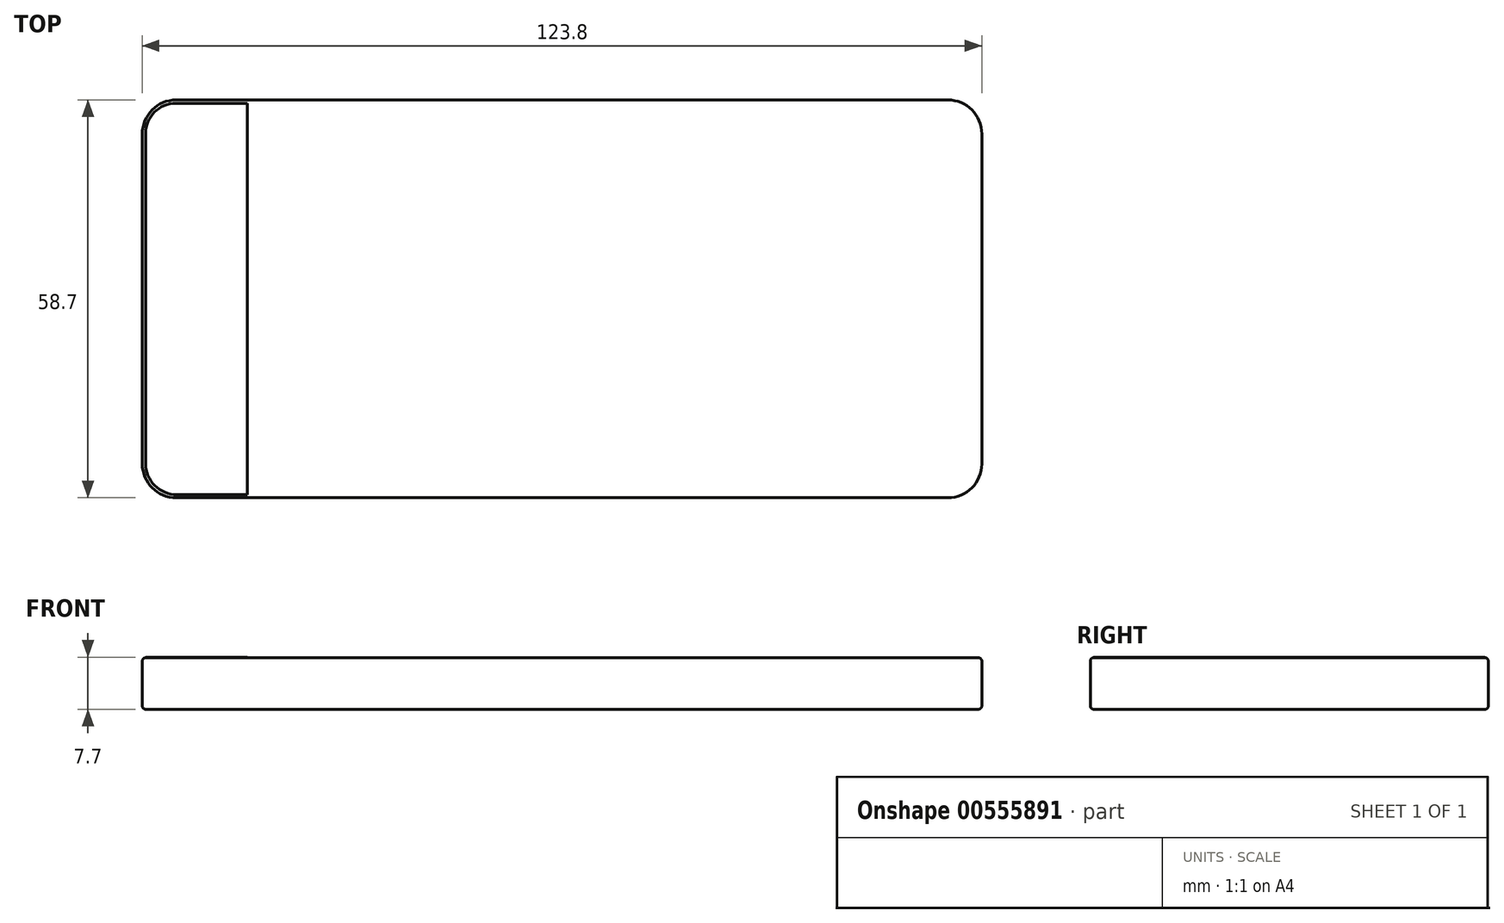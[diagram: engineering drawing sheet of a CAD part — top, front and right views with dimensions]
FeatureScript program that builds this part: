
annotation { "Feature Type Name" : "Feature", "Feature Type Description" : "" }
export const myFeature = defineFeature(function(context is Context, id is Id, definition is map)
    precondition{}
    {
        {
            var Q0;
            Q0=qCreatedBy(makeId("Top.planeOp"),FACE);
            var sketch = newSketch(context, id + "F0", { "sketchPlane" : qUnion([Q0])});
            skLineSegment(sketch, "E0.bottom", {"start": v(-53.09, -10.18) * mm, "end": v(60.71, -10.18) * mm});
            skLineSegment(sketch, "E0.top", {"start": v(-53.09, 48.52) * mm, "end": v(60.71, 48.52) * mm});
            skLineSegment(sketch, "E0.left", {"start": v(-58.09, -5.18) * mm, "end": v(-58.09, 43.52) * mm});
            skLineSegment(sketch, "E0.right", {"start": v(65.71, -5.18) * mm, "end": v(65.71, 43.52) * mm});
            skPoint(sketch, "E1.visualSharp", {"position": v(-58.09, -10.18) * mm});
            skArc(sketch, "E1.filletArc", {"start": v(-58.09, -5.18) * mm, "mid": v(-56.62, -8.71) * mm, "end": v(-53.09, -10.18) * mm});
            skPoint(sketch, "E2.visualSharp", {"position": v(-58.09, 48.52) * mm});
            skArc(sketch, "E2.filletArc", {"start": v(-53.09, 48.52) * mm, "mid": v(-56.62, 47.06) * mm, "end": v(-58.09, 43.52) * mm});
            skPoint(sketch, "E3.visualSharp", {"position": v(65.71, 48.52) * mm});
            skArc(sketch, "E3.filletArc", {"start": v(65.71, 43.52) * mm, "mid": v(64.25, 47.06) * mm, "end": v(60.71, 48.52) * mm});
            skPoint(sketch, "E4.visualSharp", {"position": v(65.71, -10.18) * mm});
            skArc(sketch, "E4.filletArc", {"start": v(60.71, -10.18) * mm, "mid": v(64.25, -8.71) * mm, "end": v(65.71, -5.18) * mm});
            skSolve(sketch);
        }
        {
            var Q0;
            Q0=makeQuery(id+"F0.imprint","IMPRINT",FACE,{"disambiguationData":[TD([[makeQuery(id+"F0.imprint","IMPRINT",EDGE,{"derivedFrom":sQuery(id+"F0.wireOp",EDGE,"E0.bottom")}),1.0]])]});
            extrude(context, id + "F1", {"entities" : qUnion([Q0]), "depth" : 7.6 * mm, "offsetDistance" : 25 * mm});
        }
        {
            var Q0;
            Q0=makeQuery(id+"F1.opExtrude","CAP_FACE",FACE,{"disambiguationData":[OSD([sQuery(id+"F0.wireOp",EDGE,"E0.bottom"),sQuery(id+"F0.wireOp",EDGE,"E0.top"),sQuery(id+"F0.wireOp",EDGE,"E0.left"),sQuery(id+"F0.wireOp",EDGE,"E0.right"),sQuery(id+"F0.wireOp",EDGE,"E1.filletArc"),sQuery(id+"F0.wireOp",EDGE,"E2.filletArc"),sQuery(id+"F0.wireOp",EDGE,"E3.filletArc"),sQuery(id+"F0.wireOp",EDGE,"E4.filletArc")])],"isStart":false});
            fillet(context, id + "F2", {"entities" : qUnion([Q0]), "radius" : .5 * mm, "tangentPropagation" : true, "allowEdgeOverflow" : false});
        }
        {
            var Q0;
            Q0=makeQuery(id+"F1.opExtrude","CAP_FACE",FACE,{"disambiguationData":[OSD([sQuery(id+"F0.wireOp",EDGE,"E0.bottom"),sQuery(id+"F0.wireOp",EDGE,"E0.top"),sQuery(id+"F0.wireOp",EDGE,"E0.left"),sQuery(id+"F0.wireOp",EDGE,"E0.right"),sQuery(id+"F0.wireOp",EDGE,"E1.filletArc"),sQuery(id+"F0.wireOp",EDGE,"E2.filletArc"),sQuery(id+"F0.wireOp",EDGE,"E3.filletArc"),sQuery(id+"F0.wireOp",EDGE,"E4.filletArc")])],"isStart":true});
            fillet(context, id + "F3", {"entities" : qUnion([Q0]), "radius" : 0.5 * mm, "tangentPropagation" : true, "allowEdgeOverflow" : false});
        }
        {
            var Q0;
            Q0=makeQuery(id+"F1.opExtrude","CAP_FACE",FACE,{"disambiguationData":[OSD([sQuery(id+"F0.wireOp",EDGE,"E0.bottom"),sQuery(id+"F0.wireOp",EDGE,"E0.top"),sQuery(id+"F0.wireOp",EDGE,"E0.left"),sQuery(id+"F0.wireOp",EDGE,"E0.right"),sQuery(id+"F0.wireOp",EDGE,"E1.filletArc"),sQuery(id+"F0.wireOp",EDGE,"E2.filletArc"),sQuery(id+"F0.wireOp",EDGE,"E3.filletArc"),sQuery(id+"F0.wireOp",EDGE,"E4.filletArc")])],"isStart":false});
            var sketch = newSketch(context, id + "F4", { "sketchPlane" : qUnion([Q0])});
            skLineSegment(sketch, "E5.bottom", {"start": v(-53, -9.7) * mm, "end": v(-42.6, -9.7) * mm});
            skLineSegment(sketch, "E5.top", {"start": v(-53.14, 48.02) * mm, "end": v(-42.6, 48.02) * mm});
            skLineSegment(sketch, "E5.left", {"start": v(-57.6, -5.1) * mm, "end": v(-57.6, 43.57) * mm});
            skLineSegment(sketch, "E5.right", {"start": v(-42.6, -9.7) * mm, "end": v(-42.6, 48.02) * mm});
            skPoint(sketch, "E6.visualSharp", {"position": v(-57.6, -9.7) * mm});
            skArc(sketch, "E6.filletArc", {"start": v(-57.6, -5.1) * mm, "mid": v(-56.25, -8.36) * mm, "end": v(-53, -9.7) * mm});
            skPoint(sketch, "E7.visualSharp", {"position": v(-57.6, 48.02) * mm});
            skArc(sketch, "E7.filletArc", {"start": v(-53.14, 48.02) * mm, "mid": v(-56.3, 46.72) * mm, "end": v(-57.6, 43.57) * mm});
            skSolve(sketch);
        }
        {
            var Q0;
            Q0 = qSketchRegion(id + "F4", true);
            extrude(context, id + "F5", {"entities" : qUnion([Q0]), "operationType" : NewBodyOperationType.ADD, "depth" : 0.1 * mm, "offsetDistance" : 25 * mm});
        }
    });
